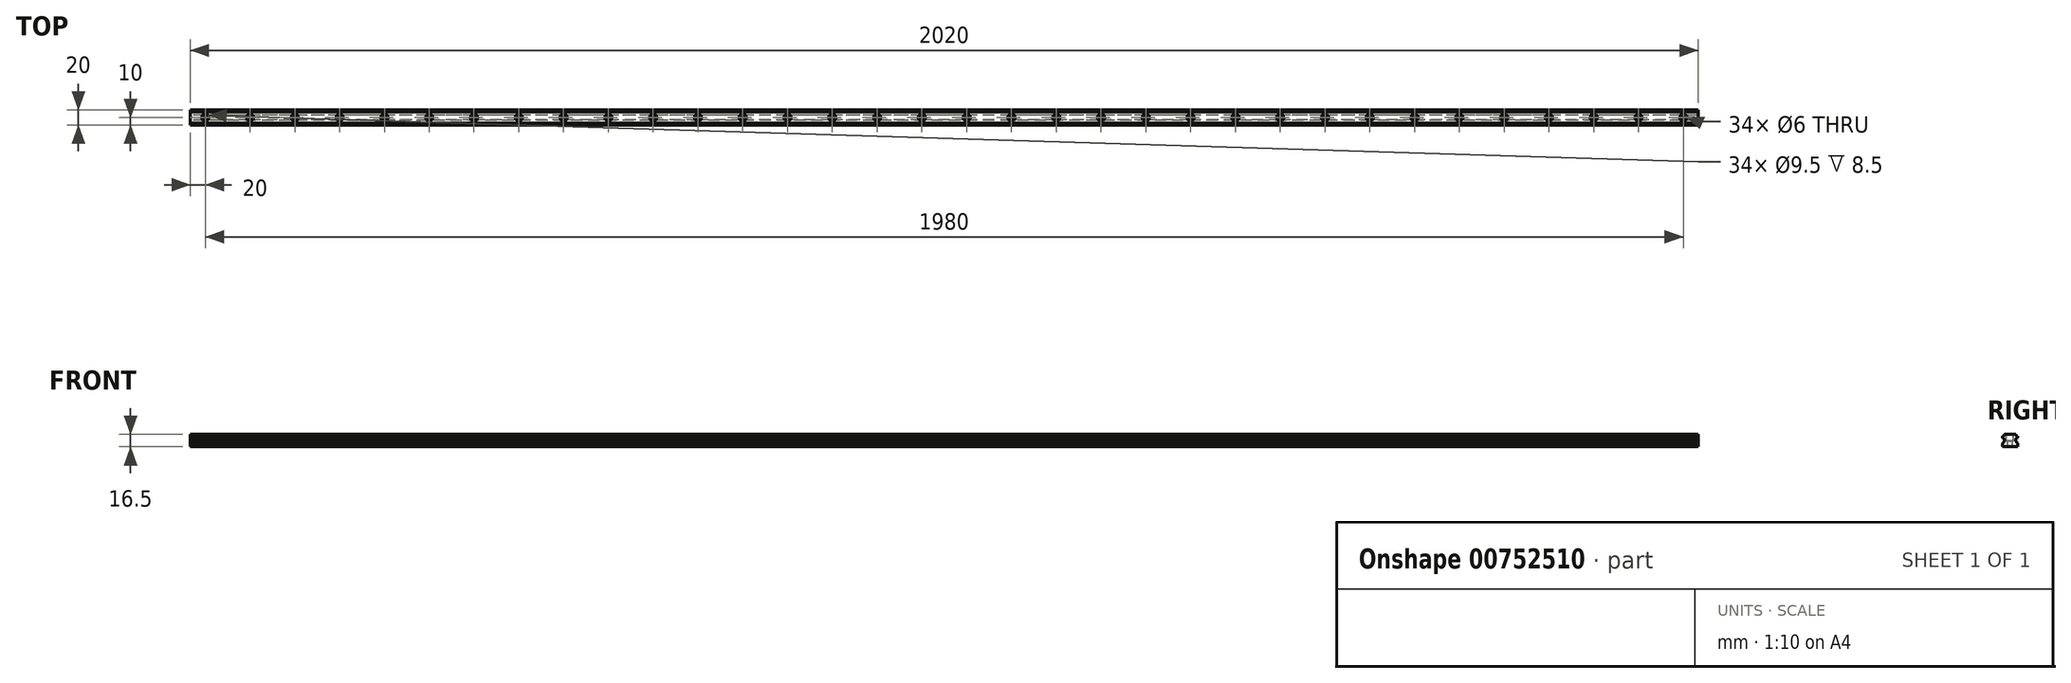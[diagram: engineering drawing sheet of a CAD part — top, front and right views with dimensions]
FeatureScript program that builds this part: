
annotation { "Feature Type Name" : "Feature", "Feature Type Description" : "" }
export const myFeature = defineFeature(function(context is Context, id is Id, definition is map)
    precondition{}
    {
        {
            var Q0;
            Q0=qCreatedBy(makeId("Right.planeOp"),FACE);
            var sketch = newSketch(context, id + "F0", { "sketchPlane" : qUnion([Q0])});
            skLineSegment(sketch, "E0", {"start": v(0, 0.5) * mm, "end": v(3, 0.5) * mm});
            skLineSegment(sketch, "E1", {"start": v(3, 0.5) * mm, "end": v(3.5, 0) * mm});
            skLineSegment(sketch, "E2", {"start": v(3.5, 0) * mm, "end": v(9.5, 0) * mm});
            skLineSegment(sketch, "E3", {"start": v(9.5, 0) * mm, "end": v(10, 0.5) * mm});
            skLineSegment(sketch, "E4", {"start": v(10, 0.5) * mm, "end": v(10, 4.6) * mm});
            skLineSegment(sketch, "E5", {"start": v(10, 4.6) * mm, "end": v(7.53, 7.07) * mm});
            skLineSegment(sketch, "E6", {"start": v(7.53, 7.07) * mm, "end": v(7.53, 9.55) * mm});
            skLineSegment(sketch, "E7", {"start": v(7.53, 9.55) * mm, "end": v(7.7, 9.73) * mm});
            skLineSegment(sketch, "E8", {"start": v(10, 12.03) * mm, "end": v(10, 14.03) * mm});
            skLineSegment(sketch, "E9", {"start": v(10, 14.03) * mm, "end": v(9.82, 14.2) * mm});
            skLineSegment(sketch, "E10", {"start": v(7.53, 16.5) * mm, "end": v(0, 16.5) * mm});
            skLineSegment(sketch, "E11", {"start": v(0, 16.5) * mm, "end": v(0, 0) * mm, "construction": true});
            skArc(sketch, "E12", {"start": v(7.7, 16.32) * mm, "mid": v(8.4, 14.9) * mm, "end": v(9.82, 14.2) * mm});
            skLineSegment(sketch, "E13", {"start": v(7.7, 16.32) * mm, "end": v(7.53, 16.5) * mm});
            skLineSegment(sketch, "E14", {"start": v(9.82, 14.2) * mm, "end": v(7.7, 16.32) * mm, "construction": true});
            skLineSegment(sketch, "E15", {"start": v(9.82, 11.85) * mm, "end": v(10, 12.03) * mm});
            skLineSegment(sketch, "E16", {"start": v(7.7, 9.73) * mm, "end": v(9.82, 11.85) * mm, "construction": true});
            skArc(sketch, "E17", {"start": v(9.82, 11.85) * mm, "mid": v(8.4, 11.14) * mm, "end": v(7.7, 9.73) * mm});
            skLineSegment(sketch, "E18.MirrorCS", {"start": v(-9.82, 11.85) * mm, "end": v(-10, 12.03) * mm});
            skLineSegment(sketch, "E19.MirrorCS", {"start": v(-7.7, 16.32) * mm, "end": v(-7.53, 16.5) * mm});
            skLineSegment(sketch, "E20.MirrorCS", {"start": v(-7.53, 9.55) * mm, "end": v(-7.7, 9.73) * mm});
            skLineSegment(sketch, "E21.MirrorCS", {"start": v(-10, 14.03) * mm, "end": v(-9.82, 14.2) * mm});
            skLineSegment(sketch, "E22.MirrorCS", {"start": v(-3, 0.5) * mm, "end": v(-3.5, 0) * mm});
            skLineSegment(sketch, "E23.MirrorCS", {"start": v(-9.5, 0) * mm, "end": v(-10, 0.5) * mm});
            skLineSegment(sketch, "E24.MirrorCS", {"start": v(-9.82, 14.2) * mm, "end": v(-7.7, 16.32) * mm, "construction": true});
            skLineSegment(sketch, "E25.MirrorCS", {"start": v(0, 0.5) * mm, "end": v(-3, 0.5) * mm});
            skLineSegment(sketch, "E26.MirrorCS", {"start": v(-7.7, 9.73) * mm, "end": v(-9.82, 11.85) * mm, "construction": true});
            skArc(sketch, "E27.MirrorCS", {"start": v(-9.82, 11.85) * mm, "mid": v(-8.4, 11.14) * mm, "end": v(-7.7, 9.73) * mm});
            skLineSegment(sketch, "E28.MirrorCS", {"start": v(-7.53, 16.5) * mm, "end": v(0, 16.5) * mm});
            skArc(sketch, "E29.MirrorCS", {"start": v(-7.7, 16.32) * mm, "mid": v(-8.4, 14.9) * mm, "end": v(-9.82, 14.2) * mm});
            skLineSegment(sketch, "E30.MirrorCS", {"start": v(-10, 0.5) * mm, "end": v(-10, 4.6) * mm});
            skLineSegment(sketch, "E31.MirrorCS", {"start": v(-10, 4.6) * mm, "end": v(-7.53, 7.07) * mm});
            skLineSegment(sketch, "E32.MirrorCS", {"start": v(-10, 12.03) * mm, "end": v(-10, 14.03) * mm});
            skLineSegment(sketch, "E33.MirrorCS", {"start": v(-3.5, 0) * mm, "end": v(-9.5, 0) * mm});
            skLineSegment(sketch, "E34.MirrorCS", {"start": v(-7.53, 7.07) * mm, "end": v(-7.53, 9.55) * mm});
            skSolve(sketch);
        }
        {
            var Q0;
            Q0 = qSketchRegion(id + "F0", true);
            extrude(context, id + "F1", {"entities" : qUnion([Q0]), "depth" : 2020 * mm, "offsetDistance" : 25 * mm});
        }
        {
            var Q0;
            Q0=makeQuery(id+"F1.opExtrude","SWEPT_FACE",FACE,{"disambiguationData":[OSD([sQuery(id+"F0.wireOp",EDGE,"E10"),sQuery(id+"F0.wireOp",EDGE,"E28.MirrorCS")])]});
            var sketch = newSketch(context, id + "F2", { "sketchPlane" : qUnion([Q0])});
            skPoint(sketch, "E35", {"position": v(20, 0) * mm});
            skPoint(sketch, "E36.1.0.0", {"position": v(80, 0) * mm});
            skPoint(sketch, "E36.2.0.0", {"position": v(140, 0) * mm});
            skPoint(sketch, "E36.3.0.0", {"position": v(200, 0) * mm});
            skPoint(sketch, "E36.4.0.0", {"position": v(260, 0) * mm});
            skPoint(sketch, "E36.5.0.0", {"position": v(320, 0) * mm});
            skPoint(sketch, "E36.6.0.0", {"position": v(380, 0) * mm});
            skPoint(sketch, "E36.7.0.0", {"position": v(440, 0) * mm});
            skPoint(sketch, "E36.8.0.0", {"position": v(500, 0) * mm});
            skPoint(sketch, "E36.9.0.0", {"position": v(560, 0) * mm});
            skPoint(sketch, "E36.10.0.0", {"position": v(620, 0) * mm});
            skPoint(sketch, "E36.11.0.0", {"position": v(680, 0) * mm});
            skPoint(sketch, "E36.12.0.0", {"position": v(740, 0) * mm});
            skPoint(sketch, "E36.13.0.0", {"position": v(800, 0) * mm});
            skPoint(sketch, "E36.14.0.0", {"position": v(860, 0) * mm});
            skPoint(sketch, "E36.15.0.0", {"position": v(920, 0) * mm});
            skPoint(sketch, "E36.16.0.0", {"position": v(980, 0) * mm});
            skPoint(sketch, "E36.17.0.0", {"position": v(1040, 0) * mm});
            skPoint(sketch, "E36.18.0.0", {"position": v(1100, 0) * mm});
            skPoint(sketch, "E36.19.0.0", {"position": v(1160, 0) * mm});
            skPoint(sketch, "E36.20.0.0", {"position": v(1220, 0) * mm});
            skPoint(sketch, "E36.21.0.0", {"position": v(1280, 0) * mm});
            skPoint(sketch, "E36.22.0.0", {"position": v(1340, 0) * mm});
            skPoint(sketch, "E36.23.0.0", {"position": v(1400, 0) * mm});
            skPoint(sketch, "E36.24.0.0", {"position": v(1460, 0) * mm});
            skPoint(sketch, "E36.25.0.0", {"position": v(1520, 0) * mm});
            skPoint(sketch, "E36.26.0.0", {"position": v(1580, 0) * mm});
            skPoint(sketch, "E36.27.0.0", {"position": v(1640, 0) * mm});
            skPoint(sketch, "E36.28.0.0", {"position": v(1700, 0) * mm});
            skPoint(sketch, "E36.29.0.0", {"position": v(1760, 0) * mm});
            skPoint(sketch, "E36.30.0.0", {"position": v(1820, 0) * mm});
            skPoint(sketch, "E36.31.0.0", {"position": v(1880, 0) * mm});
            skPoint(sketch, "E36.32.0.0", {"position": v(1940, 0) * mm});
            skPoint(sketch, "E36.33.0.0", {"position": v(2000, 0) * mm});
            skPoint(sketch, "E36.34.0.0", {"position": v(2060, 0) * mm});
            skPoint(sketch, "E36.35.0.0", {"position": v(2120, 0) * mm});
            skPoint(sketch, "E36.36.0.0", {"position": v(2180, 0) * mm});
            skPoint(sketch, "E36.37.0.0", {"position": v(2240, 0) * mm});
            skPoint(sketch, "E36.38.0.0", {"position": v(2300, 0) * mm});
            skPoint(sketch, "E36.39.0.0", {"position": v(2360, 0) * mm});
            skPoint(sketch, "E36.40.0.0", {"position": v(2420, 0) * mm});
            skPoint(sketch, "E36.41.0.0", {"position": v(2480, 0) * mm});
            skPoint(sketch, "E36.42.0.0", {"position": v(2540, 0) * mm});
            skPoint(sketch, "E36.43.0.0", {"position": v(2600, 0) * mm});
            skPoint(sketch, "E36.44.0.0", {"position": v(2660, 0) * mm});
            skLineSegment(sketch, "E36.direction1", {"start": v(20, 0) * mm, "end": v(80, 0) * mm, "construction": true});
            skSolve(sketch);
        }
        {
            var Q0;
            Q0=sQuery(id+"F2.wireOp",VERTEX,"E35");
            var Q1;
            Q1=sQuery(id+"F2.wireOp",VERTEX,"E36.1.0.0");
            var Q2;
            Q2=sQuery(id+"F2.wireOp",VERTEX,"E36.2.0.0");
            var Q3;
            Q3=sQuery(id+"F2.wireOp",VERTEX,"E36.3.0.0");
            var Q4;
            Q4=sQuery(id+"F2.wireOp",VERTEX,"E36.4.0.0");
            var Q5;
            Q5=sQuery(id+"F2.wireOp",VERTEX,"E36.5.0.0");
            var Q6;
            Q6=sQuery(id+"F2.wireOp",VERTEX,"E36.6.0.0");
            var Q7;
            Q7=sQuery(id+"F2.wireOp",VERTEX,"E36.8.0.0");
            var Q8;
            Q8=sQuery(id+"F2.wireOp",VERTEX,"E36.7.0.0");
            var Q9;
            Q9=sQuery(id+"F2.wireOp",VERTEX,"E36.9.0.0");
            var Q10;
            Q10=sQuery(id+"F2.wireOp",VERTEX,"E36.10.0.0");
            var Q11;
            Q11=sQuery(id+"F2.wireOp",VERTEX,"E36.11.0.0");
            var Q12;
            Q12=sQuery(id+"F2.wireOp",VERTEX,"E36.12.0.0");
            var Q13;
            Q13=sQuery(id+"F2.wireOp",VERTEX,"E36.13.0.0");
            var Q14;
            Q14=sQuery(id+"F2.wireOp",VERTEX,"E36.14.0.0");
            var Q15;
            Q15=sQuery(id+"F2.wireOp",VERTEX,"E36.15.0.0");
            var Q16;
            Q16=sQuery(id+"F2.wireOp",VERTEX,"E36.16.0.0");
            var Q17;
            Q17=sQuery(id+"F2.wireOp",VERTEX,"E36.17.0.0");
            var Q18;
            Q18=sQuery(id+"F2.wireOp",VERTEX,"E36.18.0.0");
            var Q19;
            Q19=sQuery(id+"F2.wireOp",VERTEX,"E36.19.0.0");
            var Q20;
            Q20=sQuery(id+"F2.wireOp",VERTEX,"E36.20.0.0");
            var Q21;
            Q21=sQuery(id+"F2.wireOp",VERTEX,"E36.21.0.0");
            var Q22;
            Q22=sQuery(id+"F2.wireOp",VERTEX,"E36.22.0.0");
            var Q23;
            Q23=sQuery(id+"F2.wireOp",VERTEX,"E36.23.0.0");
            var Q24;
            Q24=sQuery(id+"F2.wireOp",VERTEX,"E36.24.0.0");
            var Q25;
            Q25=sQuery(id+"F2.wireOp",VERTEX,"E36.25.0.0");
            var Q26;
            Q26=sQuery(id+"F2.wireOp",VERTEX,"E36.26.0.0");
            var Q27;
            Q27=sQuery(id+"F2.wireOp",VERTEX,"E36.27.0.0");
            var Q28;
            Q28=sQuery(id+"F2.wireOp",VERTEX,"E36.28.0.0");
            var Q29;
            Q29=sQuery(id+"F2.wireOp",VERTEX,"E36.29.0.0");
            var Q30;
            Q30=sQuery(id+"F2.wireOp",VERTEX,"E36.30.0.0");
            var Q31;
            Q31=sQuery(id+"F2.wireOp",VERTEX,"E36.31.0.0");
            var Q32;
            Q32=sQuery(id+"F2.wireOp",VERTEX,"E36.32.0.0");
            var Q33;
            Q33=sQuery(id+"F2.wireOp",VERTEX,"E36.33.0.0");
            var Q34;
            Q34=makeQuery(id+"F1.opExtrude","SWEPT_BODY",BODY,{"disambiguationData":[OSD([sQuery(id+"F0.wireOp",EDGE,"E0"),sQuery(id+"F0.wireOp",EDGE,"E1"),sQuery(id+"F0.wireOp",EDGE,"E2"),sQuery(id+"F0.wireOp",EDGE,"E3"),sQuery(id+"F0.wireOp",EDGE,"E4"),sQuery(id+"F0.wireOp",EDGE,"E5"),sQuery(id+"F0.wireOp",EDGE,"E6"),sQuery(id+"F0.wireOp",EDGE,"E7"),sQuery(id+"F0.wireOp",EDGE,"E8"),sQuery(id+"F0.wireOp",EDGE,"E9"),sQuery(id+"F0.wireOp",EDGE,"E10"),sQuery(id+"F0.wireOp",EDGE,"E12"),sQuery(id+"F0.wireOp",EDGE,"E13"),sQuery(id+"F0.wireOp",EDGE,"E15"),sQuery(id+"F0.wireOp",EDGE,"E17"),sQuery(id+"F0.wireOp",EDGE,"E18.MirrorCS"),sQuery(id+"F0.wireOp",EDGE,"E19.MirrorCS"),sQuery(id+"F0.wireOp",EDGE,"E20.MirrorCS"),sQuery(id+"F0.wireOp",EDGE,"E21.MirrorCS"),sQuery(id+"F0.wireOp",EDGE,"E22.MirrorCS"),sQuery(id+"F0.wireOp",EDGE,"E23.MirrorCS"),sQuery(id+"F0.wireOp",EDGE,"E25.MirrorCS"),sQuery(id+"F0.wireOp",EDGE,"E27.MirrorCS"),sQuery(id+"F0.wireOp",EDGE,"E28.MirrorCS"),sQuery(id+"F0.wireOp",EDGE,"E29.MirrorCS"),sQuery(id+"F0.wireOp",EDGE,"E30.MirrorCS"),sQuery(id+"F0.wireOp",EDGE,"E31.MirrorCS"),sQuery(id+"F0.wireOp",EDGE,"E32.MirrorCS"),sQuery(id+"F0.wireOp",EDGE,"E33.MirrorCS"),sQuery(id+"F0.wireOp",EDGE,"E34.MirrorCS")])]});
            hole(context, id + "F3", {"style" : HoleStyle.C_BORE, "endStyle" : HoleEndStyle.THROUGH, "holeDiameter" : 6 * mm, "cBoreDiameter" : 9.5 * mm, "cBoreDepth" : 8.5 * mm, "majorDiameter" : 5 * mm, "isTappedThrough" : true, "tappedDepth" : 12 * mm, "tapClearance" : 3, "startFromSketch" : true, "locations" : qUnion([Q0, Q1, Q2, Q3, Q4, Q5, Q6, Q7, Q8, Q9, Q10, Q11, Q12, Q13, Q14, Q15, Q16, Q17, Q18, Q19, Q20, Q21, Q22, Q23, Q24, Q25, Q26, Q27, Q28, Q29, Q30, Q31, Q32, Q33]), "scope" : qUnion([Q34])});
        }
    });
